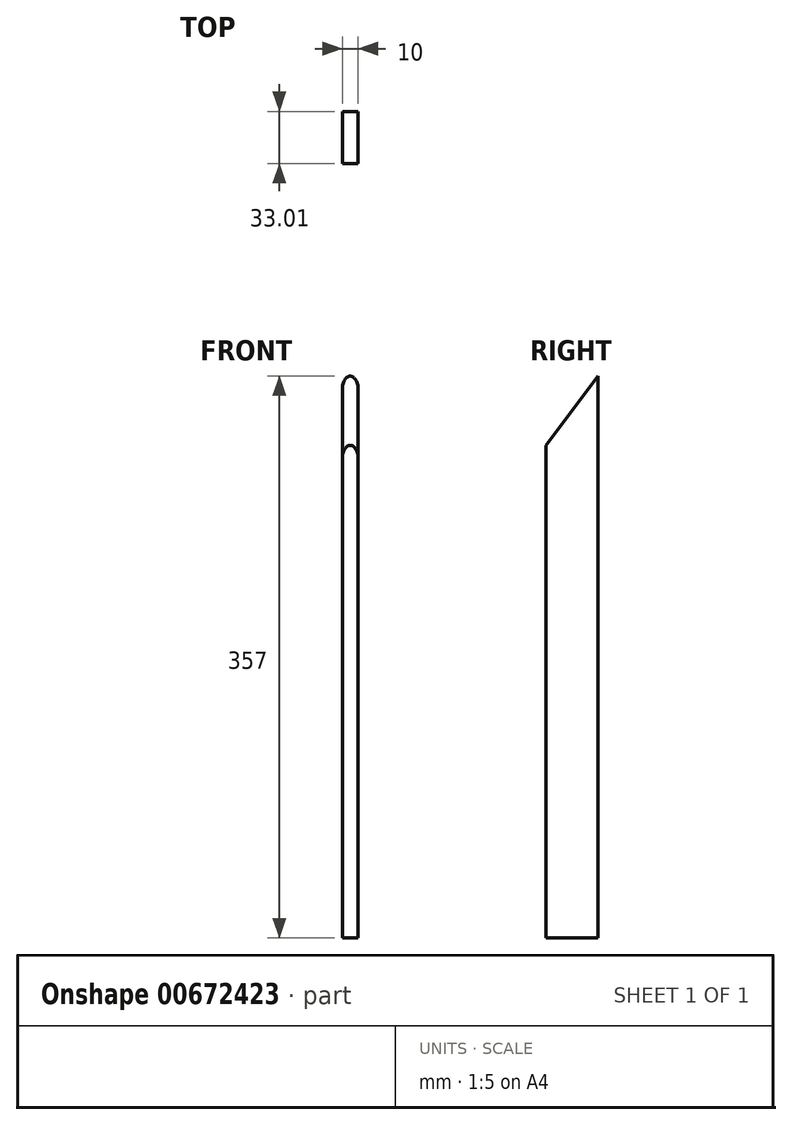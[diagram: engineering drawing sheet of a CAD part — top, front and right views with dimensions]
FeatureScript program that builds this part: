
annotation { "Feature Type Name" : "Feature", "Feature Type Description" : "" }
export const myFeature = defineFeature(function(context is Context, id is Id, definition is map)
    precondition{}
    {
        {
            var Q0;
            Q0=qCreatedBy(makeId("Right.planeOp"),FACE);
            var sketch = newSketch(context, id + "F0", { "sketchPlane" : qUnion([Q0])});
            skLineSegment(sketch, "E0.bottom", {"start": v(-56.57, 0) * mm, "end": v(-42.08, 0) * mm});
            skLineSegment(sketch, "E0.top", {"start": v(-56.57, 313) * mm, "end": v(-42.08, 313) * mm});
            skLineSegment(sketch, "E0.left", {"start": v(-56.57, 0) * mm, "end": v(-56.57, 313) * mm});
            skLineSegment(sketch, "E0.right", {"start": v(-42.08, 0) * mm, "end": v(-42.08, 313) * mm});
            skLineSegment(sketch, "E1", {"start": v(-23.56, 0) * mm, "end": v(-23.56, 357) * mm});
            skLineSegment(sketch, "E2", {"start": v(-23.56, 357) * mm, "end": v(-56.57, 313) * mm});
            skLineSegment(sketch, "E3", {"start": v(-42.08, 0) * mm, "end": v(-23.56, 0) * mm});
            skSolve(sketch);
        }
        {
            var Q0;
            Q0=qSketchRegion(id+"F0",true);
            extrude(context, id + "F1", {"entities" : qUnion([Q0]), "depth" : 10 * mm, "offsetDistance" : 25 * mm});
        }
        {
            var Q0;
            Q0=makeQuery(id+"F1.opExtrude","CAP_EDGE",EDGE,{"disambiguationData":[OSD([sQuery(id+"F0.wireOp",EDGE,"E2")])],"isStart":false});
            var Q1;
            Q1=makeQuery(id+"F1.opExtrude","CAP_EDGE",EDGE,{"disambiguationData":[OSD([sQuery(id+"F0.wireOp",EDGE,"E2")])],"isStart":true});
            fillet(context, id + "F2", {"entities" : qUnion([Q0, Q1]), "radius" : 5 * mm, "tangentPropagation" : true, "allowEdgeOverflow" : false});
        }
    });
